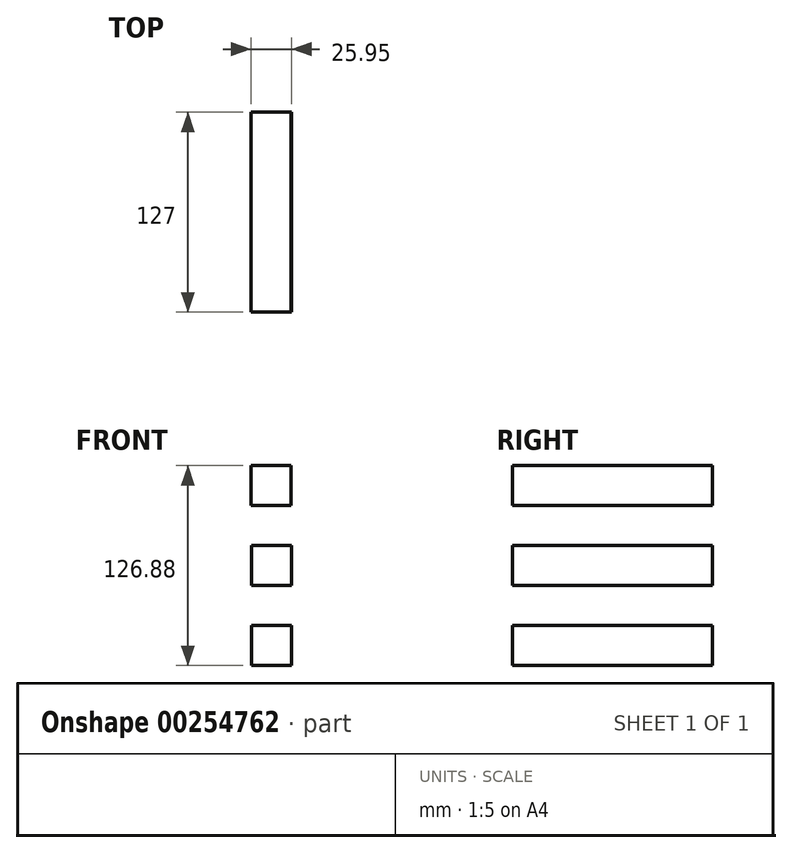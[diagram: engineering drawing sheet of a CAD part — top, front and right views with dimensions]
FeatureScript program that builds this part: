
annotation { "Feature Type Name" : "Feature", "Feature Type Description" : "" }
export const myFeature = defineFeature(function(context is Context, id is Id, definition is map)
    precondition{}
    {
        {
            var Q0;
            Q0=qCreatedBy(makeId("Front.planeOp"),FACE);
            var sketch = newSketch(context, id + "F0", { "sketchPlane" : qUnion([Q0])});
            skLineSegment(sketch, "E0.bottom", {"start": v(-13.25, 69.36) * mm, "end": v(12.15, 69.36) * mm});
            skLineSegment(sketch, "E0.top", {"start": v(-13.25, 43.96) * mm, "end": v(12.15, 43.96) * mm});
            skLineSegment(sketch, "E0.left", {"start": v(-13.25, 69.36) * mm, "end": v(-13.25, 43.96) * mm});
            skLineSegment(sketch, "E0.right", {"start": v(12.15, 69.36) * mm, "end": v(12.15, 43.96) * mm});
            skLineSegment(sketch, "E1", {"start": v(0, 56.78) * mm, "end": v(0, 5.98) * mm});
            skLineSegment(sketch, "E2.bottom", {"start": v(-12.7, 18.68) * mm, "end": v(12.7, 18.68) * mm});
            skLineSegment(sketch, "E2.top", {"start": v(-12.7, -6.72) * mm, "end": v(12.7, -6.72) * mm});
            skLineSegment(sketch, "E2.left", {"start": v(-12.7, 18.68) * mm, "end": v(-12.7, -6.72) * mm});
            skLineSegment(sketch, "E2.right", {"start": v(12.7, 18.68) * mm, "end": v(12.7, -6.72) * mm});
            skPoint(sketch, "E2.middle", {"position": v(0, 5.98) * mm});
            skLineSegment(sketch, "E3", {"start": v(0, 5.98) * mm, "end": v(0, -44.82) * mm});
            skPoint(sketch, "E3.endSnap0", {"position": v(0, -6.72) * mm});
            skLineSegment(sketch, "E4.bottom", {"start": v(-12.7, -32.12) * mm, "end": v(12.7, -32.12) * mm});
            skLineSegment(sketch, "E4.top", {"start": v(-12.7, -57.52) * mm, "end": v(12.7, -57.52) * mm});
            skLineSegment(sketch, "E4.left", {"start": v(-12.7, -32.12) * mm, "end": v(-12.7, -57.52) * mm});
            skLineSegment(sketch, "E4.right", {"start": v(12.7, -32.12) * mm, "end": v(12.7, -57.52) * mm});
            skPoint(sketch, "E4.middle", {"position": v(0, -44.82) * mm});
            skSolve(sketch);
        }
        {
            var Q0;
            Q0 = qSketchRegion(id + "F0", true);
            extrude(context, id + "F1", {"entities" : qUnion([Q0]), "endBound" : BoundingType.SYMMETRIC, "depth" : 127 * mm});
        }
    });
